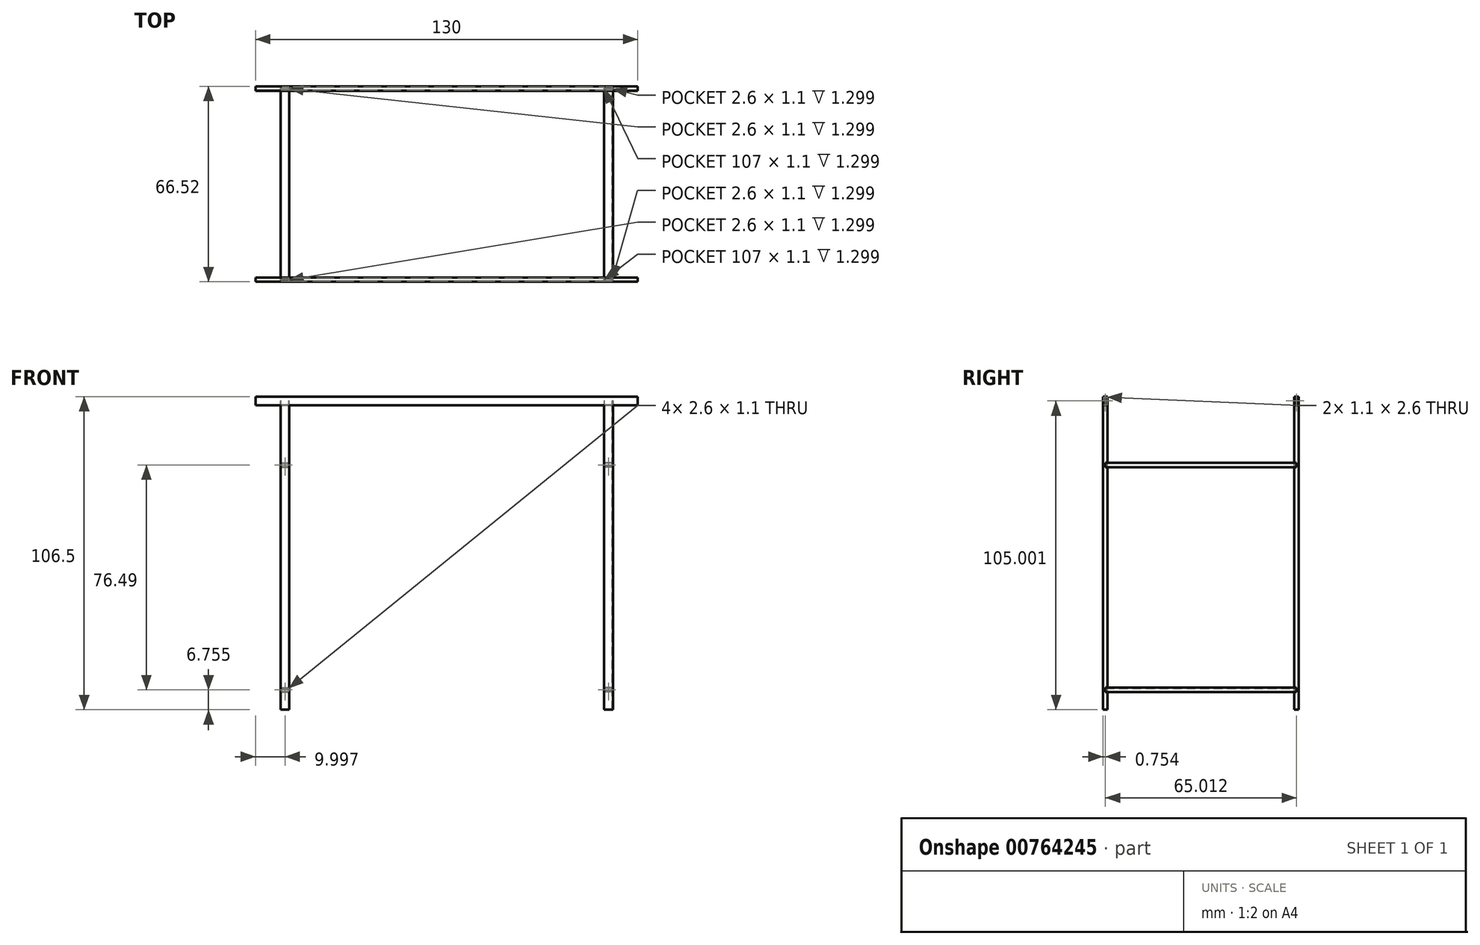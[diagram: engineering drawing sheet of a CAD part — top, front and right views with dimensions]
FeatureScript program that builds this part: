
annotation { "Feature Type Name" : "Feature", "Feature Type Description" : "" }
export const myFeature = defineFeature(function(context is Context, id is Id, definition is map)
    precondition{}
    {
        {
            var Q0;
            Q0=qCreatedBy(makeId("Top.planeOp"),FACE);
            cPlane(context, id + "F0", {"entities" : qUnion([Q0]), "cplaneType" : CPlaneType.OFFSET, "offset" : 60 * mm, "width" : 150 * mm, "height" : 150 * mm});
        }
        {
            var Q0;
            Q0=qCreatedBy(id+"F0.planeOp",FACE);
            var sketch = newSketch(context, id + "F1", { "sketchPlane" : qUnion([Q0])});
            skLineSegment(sketch, "E0", {"start": v(0, 0) * mm, "end": v(-65, 0) * mm, "construction": true});
            skLineSegment(sketch, "E1", {"start": v(-65, 0) * mm, "end": v(-65, 32.5) * mm, "construction": true});
            skSolve(sketch);
        }
        {
            var Q0;
            Q0=qCreatedBy(makeId("Right.planeOp"),FACE);
            cPlane(context, id + "F2", {"entities" : qUnion([Q0]), "cplaneType" : CPlaneType.OFFSET, "offset" : 65 * mm, "oppositeDirection" : true, "width" : 150 * mm, "height" : 150 * mm});
        }
        {
            var Q0;
            Q0=qCreatedBy(id+"F2.planeOp",FACE);
            var sketch = newSketch(context, id + "F3", { "sketchPlane" : qUnion([Q0])});
            skLineSegment(sketch, "E2.bottom", {"start": v(33.26, 61.5) * mm, "end": v(31.76, 61.5) * mm});
            skLineSegment(sketch, "E2.top", {"start": v(33.26, 58.5) * mm, "end": v(31.76, 58.5) * mm});
            skLineSegment(sketch, "E2.left", {"start": v(33.26, 61.5) * mm, "end": v(33.26, 58.5) * mm});
            skLineSegment(sketch, "E2.right", {"start": v(31.76, 61.5) * mm, "end": v(31.76, 58.5) * mm});
            skPoint(sketch, "E2.middle", {"position": v(32.5, 60) * mm});
            skLineSegment(sketch, "E3.bottom", {"start": v(33.06, 61.3) * mm, "end": v(31.96, 61.3) * mm});
            skLineSegment(sketch, "E3.top", {"start": v(33.06, 58.7) * mm, "end": v(31.96, 58.7) * mm});
            skLineSegment(sketch, "E3.left", {"start": v(33.06, 61.3) * mm, "end": v(33.06, 58.7) * mm});
            skLineSegment(sketch, "E3.right", {"start": v(31.96, 61.3) * mm, "end": v(31.96, 58.7) * mm});
            skSolve(sketch);
        }
        {
            var Q0;
            Q0=makeQuery(id+"F3.imprint","IMPRINT",FACE,{"disambiguationData":[TD([[makeQuery(id+"F3.imprint","IMPRINT",EDGE,{"derivedFrom":sQuery(id+"F3.wireOp",EDGE,"E2.bottom")}),1.0]])]});
            extrude(context, id + "F4", {"entities" : qUnion([Q0]), "depth" : 130 * mm, "offsetDistance" : 25 * mm});
        }
        {
            var Q0;
            Q0=makeQuery(id+"F4.opExtrude","SWEPT_BODY",BODY,{"disambiguationData":[OSD([sQuery(id+"F3.wireOp",EDGE,"E2.bottom"),sQuery(id+"F3.wireOp",EDGE,"E2.top"),sQuery(id+"F3.wireOp",EDGE,"E2.left"),sQuery(id+"F3.wireOp",EDGE,"E2.right"),sQuery(id+"F3.wireOp",EDGE,"E3.bottom"),sQuery(id+"F3.wireOp",EDGE,"E3.top"),sQuery(id+"F3.wireOp",EDGE,"E3.left"),sQuery(id+"F3.wireOp",EDGE,"E3.right")])]});
            var Q1;
            Q1=qCreatedBy(makeId("Front.planeOp"),FACE);
            mirror(context, id + "F5", {"entities" : qUnion([Q0]), "mirrorPlane" : qUnion([Q1])});
        }
        {
            var Q0;
            Q0=qCreatedBy(id+"F0.planeOp",FACE);
            var sketch = newSketch(context, id + "F6", { "sketchPlane" : qUnion([Q0])});
            skLineSegment(sketch, "E4", {"start": v(0, -49.29) * mm, "end": v(0, 13.23) * mm, "construction": true});
            skLineSegment(sketch, "E5", {"start": v(0, -32.5) * mm, "end": v(-55, -32.5) * mm, "construction": true});
            skLineSegment(sketch, "E6.bottom", {"start": v(-53.5, -33.25) * mm, "end": v(-56.5, -33.25) * mm});
            skLineSegment(sketch, "E6.top", {"start": v(-53.5, -31.75) * mm, "end": v(-56.5, -31.75) * mm});
            skLineSegment(sketch, "E6.left", {"start": v(-53.5, -33.25) * mm, "end": v(-53.5, -31.75) * mm});
            skLineSegment(sketch, "E6.right", {"start": v(-56.5, -33.25) * mm, "end": v(-56.5, -31.75) * mm});
            skPoint(sketch, "E6.middle", {"position": v(-55, -32.5) * mm});
            skLineSegment(sketch, "E7.bottom", {"start": v(-53.7, -33.05) * mm, "end": v(-56.3, -33.05) * mm});
            skLineSegment(sketch, "E7.top", {"start": v(-53.7, -31.95) * mm, "end": v(-56.3, -31.95) * mm});
            skLineSegment(sketch, "E7.left", {"start": v(-53.7, -33.05) * mm, "end": v(-53.7, -31.95) * mm});
            skLineSegment(sketch, "E7.right", {"start": v(-56.3, -33.05) * mm, "end": v(-56.3, -31.95) * mm});
            skSolve(sketch);
        }
        {
            var Q0;
            Q0 = qSketchRegion(id + "F6", true);
            extrude(context, id + "F7", {"entities" : qUnion([Q0]), "oppositeDirection" : true, "depth" : 105 * mm, "offsetDistance" : 25 * mm});
        }
        {
            var Q0;
            Q0=makeQuery(id+"F7.opExtrude","SWEPT_BODY",BODY,{"disambiguationData":[OSD([sQuery(id+"F6.wireOp",EDGE,"E6.bottom"),sQuery(id+"F6.wireOp",EDGE,"E6.top"),sQuery(id+"F6.wireOp",EDGE,"E6.left"),sQuery(id+"F6.wireOp",EDGE,"E6.right"),sQuery(id+"F6.wireOp",EDGE,"E7.bottom"),sQuery(id+"F6.wireOp",EDGE,"E7.top"),sQuery(id+"F6.wireOp",EDGE,"E7.left"),sQuery(id+"F6.wireOp",EDGE,"E7.right")])]});
            var Q1;
            Q1=qCreatedBy(makeId("Right.planeOp"),FACE);
            mirror(context, id + "F8", {"operationType" : NewBodyOperationType.ADD, "entities" : qUnion([Q0]), "mirrorPlane" : qUnion([Q1])});
        }
        {
            var Q0;
            Q0=makeQuery(id+"F5.opPattern","COPY",BODY,{"derivedFrom":makeQuery(id+"F4.opExtrude","SWEPT_BODY",BODY,{"disambiguationData":[OSD([sQuery(id+"F3.wireOp",EDGE,"E2.bottom"),sQuery(id+"F3.wireOp",EDGE,"E2.top"),sQuery(id+"F3.wireOp",EDGE,"E2.left"),sQuery(id+"F3.wireOp",EDGE,"E2.right"),sQuery(id+"F3.wireOp",EDGE,"E3.bottom"),sQuery(id+"F3.wireOp",EDGE,"E3.top"),sQuery(id+"F3.wireOp",EDGE,"E3.left"),sQuery(id+"F3.wireOp",EDGE,"E3.right")])]}),"instanceName":"1"});
            var Q1;
            Q1=qCreatedBy(makeId("Front.planeOp"),FACE);
            mirror(context, id + "F9", {"operationType" : NewBodyOperationType.ADD, "entities" : qUnion([Q0]), "mirrorPlane" : qUnion([Q1])});
        }
        {
            var Q0;
            Q0=qCreatedBy(makeId("Front.planeOp"),FACE);
            var sketch = newSketch(context, id + "F10", { "sketchPlane" : qUnion([Q0])});
            skLineSegment(sketch, "E8", {"start": v(53.5, 56.46) * mm, "end": v(56.5, 56.46) * mm, "construction": true});
            skLineSegment(sketch, "E9", {"start": v(55, 58.24) * mm, "end": v(55, 38.24) * mm, "construction": true});
            skPoint(sketch, "E9.startSnap0", {"position": v(55, 56.46) * mm});
            skLineSegment(sketch, "E10.bottom", {"start": v(56.5, 39) * mm, "end": v(53.5, 39) * mm});
            skLineSegment(sketch, "E10.top", {"start": v(56.5, 37.5) * mm, "end": v(53.5, 37.5) * mm});
            skLineSegment(sketch, "E10.left", {"start": v(56.5, 39) * mm, "end": v(56.5, 37.5) * mm});
            skLineSegment(sketch, "E10.right", {"start": v(53.5, 39) * mm, "end": v(53.5, 37.5) * mm});
            skPoint(sketch, "E10.middle", {"position": v(55, 38.24) * mm});
            skLineSegment(sketch, "E11.bottom", {"start": v(56.3, 38.8) * mm, "end": v(53.7, 38.8) * mm});
            skLineSegment(sketch, "E11.top", {"start": v(56.3, 37.7) * mm, "end": v(53.7, 37.7) * mm});
            skLineSegment(sketch, "E11.left", {"start": v(56.3, 38.8) * mm, "end": v(56.3, 37.7) * mm});
            skLineSegment(sketch, "E11.right", {"start": v(53.7, 38.8) * mm, "end": v(53.7, 37.7) * mm});
            skSolve(sketch);
        }
        {
            var Q0;
            Q0 = qSketchRegion(id + "F10", true);
            extrude(context, id + "F11", {"entities" : qUnion([Q0]), "endBound" : BoundingType.SYMMETRIC, "depth" : 65 * mm, "offsetDistance" : 25 * mm});
        }
        {
            var Q0;
            Q0=makeQuery(id+"F11.opExtrude","SWEPT_BODY",BODY,{"disambiguationData":[OSD([sQuery(id+"F10.wireOp",EDGE,"E10.bottom"),sQuery(id+"F10.wireOp",EDGE,"E10.top"),sQuery(id+"F10.wireOp",EDGE,"E10.left"),sQuery(id+"F10.wireOp",EDGE,"E10.right"),sQuery(id+"F10.wireOp",EDGE,"E11.bottom"),sQuery(id+"F10.wireOp",EDGE,"E11.top"),sQuery(id+"F10.wireOp",EDGE,"E11.left"),sQuery(id+"F10.wireOp",EDGE,"E11.right")])]});
            var Q1;
            Q1=qCreatedBy(makeId("Top.planeOp"),FACE);
            mirror(context, id + "F12", {"entities" : qUnion([Q0]), "mirrorPlane" : qUnion([Q1])});
        }
        {
            var Q0;
            Q0=makeQuery(id+"F11.opExtrude","SWEPT_BODY",BODY,{"disambiguationData":[OSD([sQuery(id+"F10.wireOp",EDGE,"E10.bottom"),sQuery(id+"F10.wireOp",EDGE,"E10.top"),sQuery(id+"F10.wireOp",EDGE,"E10.left"),sQuery(id+"F10.wireOp",EDGE,"E10.right"),sQuery(id+"F10.wireOp",EDGE,"E11.bottom"),sQuery(id+"F10.wireOp",EDGE,"E11.top"),sQuery(id+"F10.wireOp",EDGE,"E11.left"),sQuery(id+"F10.wireOp",EDGE,"E11.right")])]});
            var Q1;
            Q1=qCreatedBy(makeId("Right.planeOp"),FACE);
            mirror(context, id + "F13", {"entities" : qUnion([Q0]), "mirrorPlane" : qUnion([Q1])});
        }
        {
            var Q0;
            Q0=makeQuery(id+"F13.opPattern","COPY",BODY,{"derivedFrom":makeQuery(id+"F11.opExtrude","SWEPT_BODY",BODY,{"disambiguationData":[OSD([sQuery(id+"F10.wireOp",EDGE,"E10.bottom"),sQuery(id+"F10.wireOp",EDGE,"E10.top"),sQuery(id+"F10.wireOp",EDGE,"E10.left"),sQuery(id+"F10.wireOp",EDGE,"E10.right"),sQuery(id+"F10.wireOp",EDGE,"E11.bottom"),sQuery(id+"F10.wireOp",EDGE,"E11.top"),sQuery(id+"F10.wireOp",EDGE,"E11.left"),sQuery(id+"F10.wireOp",EDGE,"E11.right")])]}),"instanceName":"1"});
            var Q1;
            Q1=qCreatedBy(makeId("Top.planeOp"),FACE);
            mirror(context, id + "F14", {"entities" : qUnion([Q0]), "mirrorPlane" : qUnion([Q1])});
        }
    });
